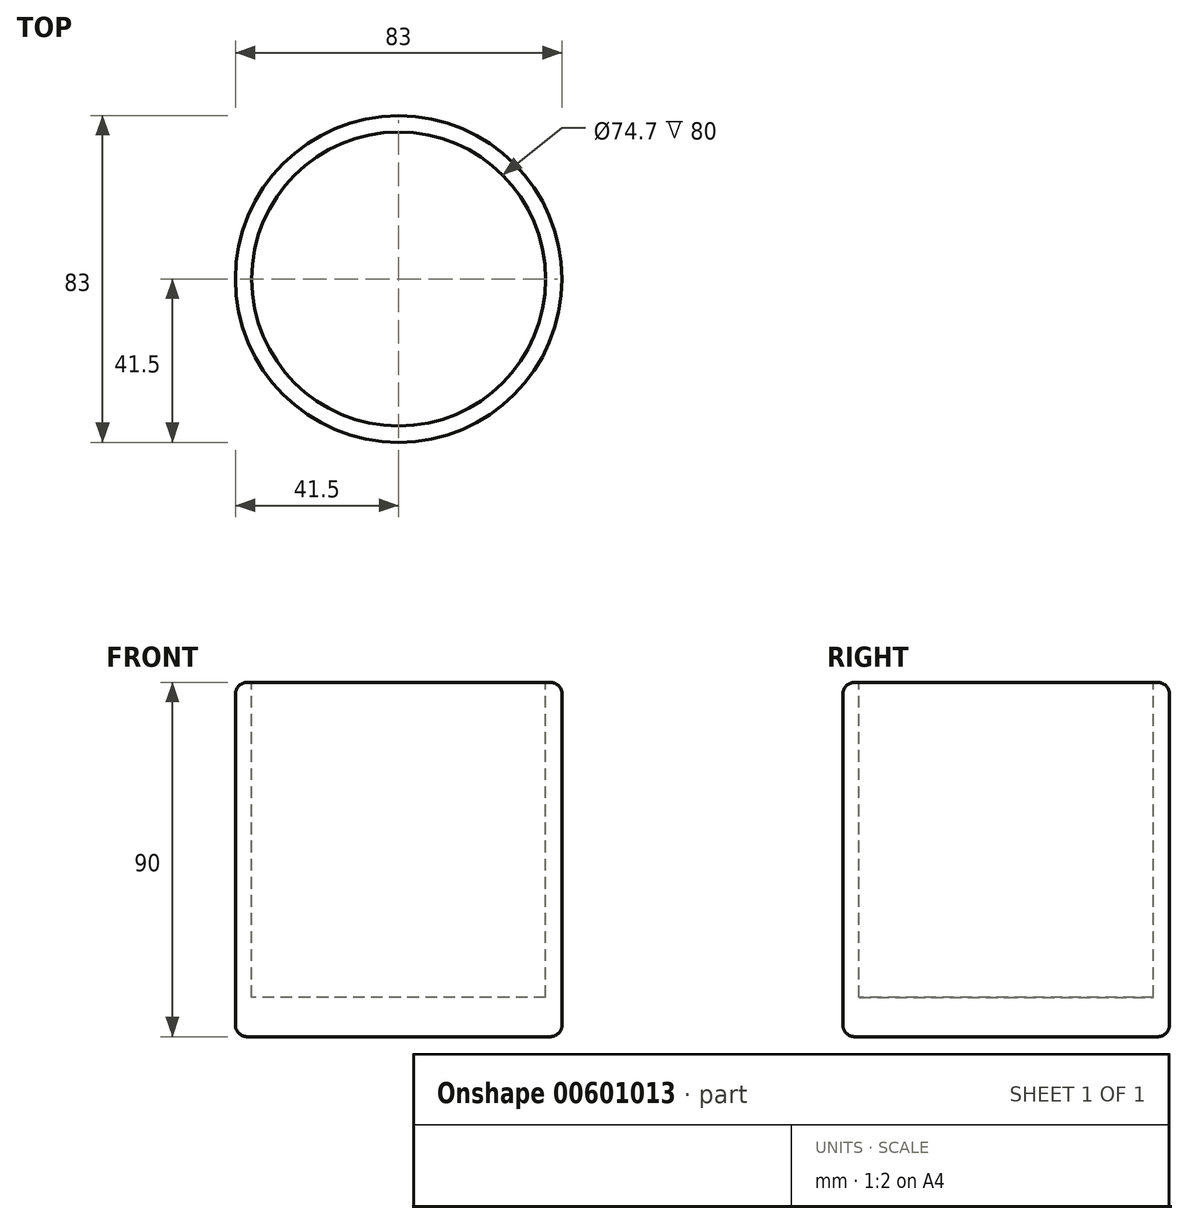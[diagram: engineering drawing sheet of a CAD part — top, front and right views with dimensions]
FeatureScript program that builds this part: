
annotation { "Feature Type Name" : "Feature", "Feature Type Description" : "" }
export const myFeature = defineFeature(function(context is Context, id is Id, definition is map)
    precondition{}
    {
        {
            var Q0;
            Q0=qCreatedBy(makeId("Top.planeOp"),FACE);
            var sketch = newSketch(context, id + "F0", { "sketchPlane" : qUnion([Q0])});
            skCircle(sketch, "E0", {"center": v(0, 0) * mm, "radius": 41.5 * mm});
            skSolve(sketch);
        }
        {
            var Q0;
            Q0 = qSketchRegion(id + "F0", true);
            extrude(context, id + "F1", {"entities" : qUnion([Q0]), "oppositeDirection" : true, "depth" : 90 * mm, "offsetDistance" : 25 * mm});
        }
        {
            var Q0;
            Q0=makeQuery(id+"F1.opExtrude","CAP_FACE",FACE,{"disambiguationData":[OSD([sQuery(id+"F0.wireOp",EDGE,"E0")])],"isStart":true});
            var sketch = newSketch(context, id + "F2", { "sketchPlane" : qUnion([Q0])});
            skCircle(sketch, "E1", {"center": v(0, 0) * mm, "radius": 37.35 * mm});
            skSolve(sketch);
        }
        {
            var Q0;
            Q0=makeQuery(id+"F2.imprint","IMPRINT",FACE,{"disambiguationData":[TD([[makeQuery(id+"F2.imprint","IMPRINT",EDGE,{"derivedFrom":sQuery(id+"F2.wireOp",EDGE,"E1")}),1.0]])]});
            extrude(context, id + "F3", {"entities" : qUnion([Q0]), "operationType" : NewBodyOperationType.REMOVE, "oppositeDirection" : true, "depth" : 80 * mm, "offsetDistance" : 25 * mm});
        }
        {
            var Q0;
            Q0=makeQuery(id+"F1.opExtrude","SWEPT_FACE",FACE,{"disambiguationData":[OSD([sQuery(id+"F0.wireOp",EDGE,"E0")])]});
            fillet(context, id + "F4", {"entities" : qUnion([Q0]), "radius" : 3 * mm, "tangentPropagation" : true, "allowEdgeOverflow" : false});
        }
    });
